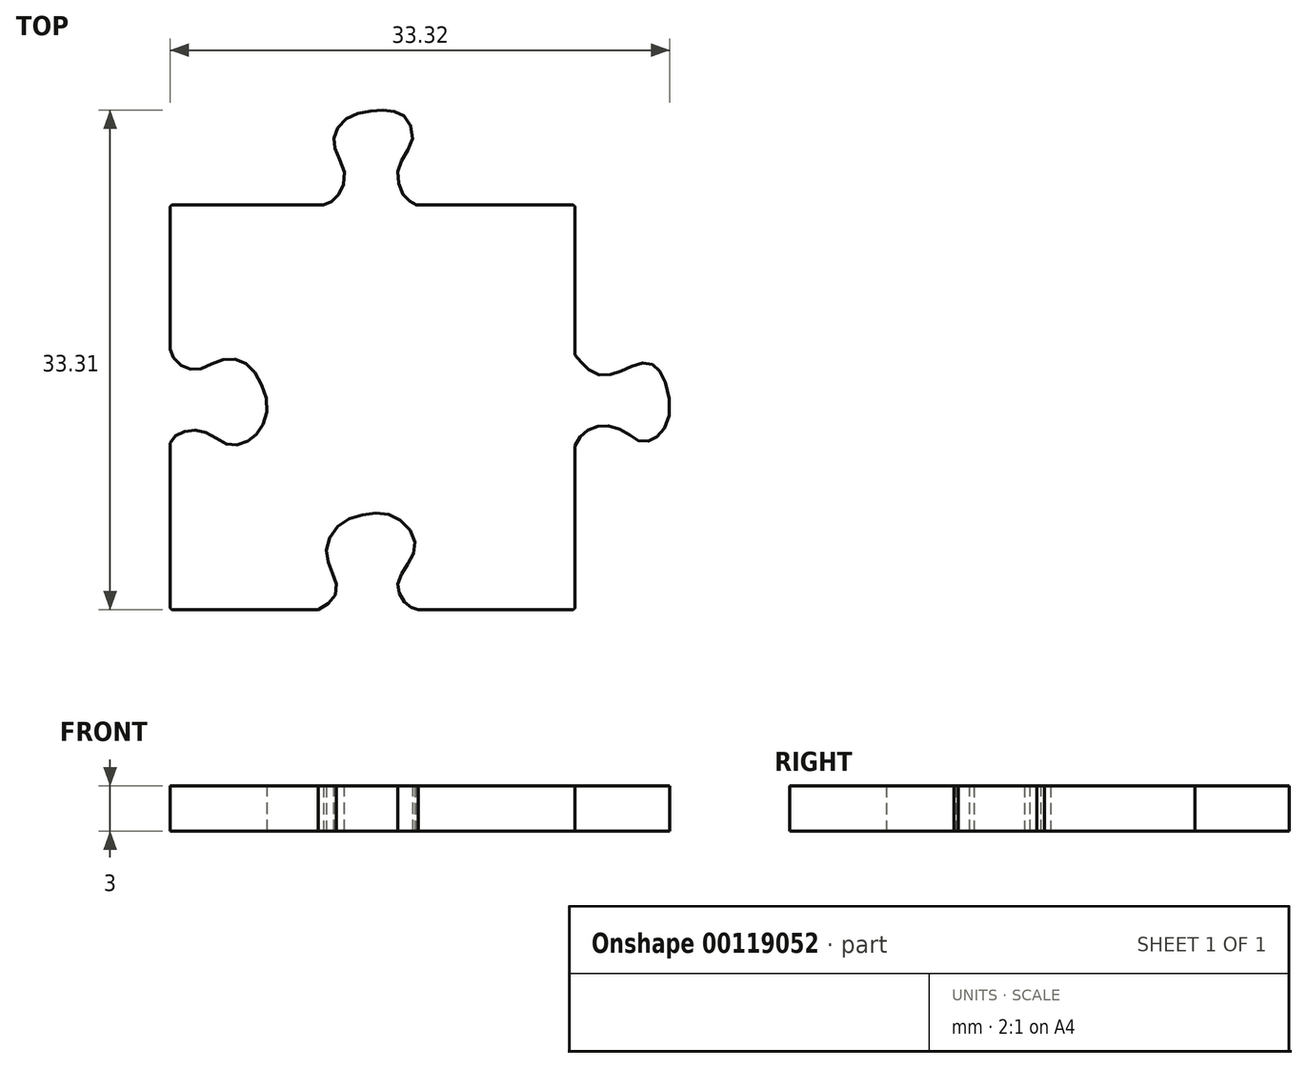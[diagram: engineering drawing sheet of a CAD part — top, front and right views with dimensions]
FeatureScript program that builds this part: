
annotation { "Feature Type Name" : "Feature", "Feature Type Description" : "" }
export const myFeature = defineFeature(function(context is Context, id is Id, definition is map)
    precondition{}
    {
        {
            var Q0;
            Q0=qCreatedBy(makeId("Top.planeOp"),FACE);
            var sketch = newSketch(context, id + "F0", { "sketchPlane" : qUnion([Q0])});
            skLineSegment(sketch, "E0.bottom", {"start": v(13.3, 13.5) * mm, "end": v(2.93, 13.5) * mm});
            skLineSegment(sketch, "E0.top", {"start": v(13.3, -13.5) * mm, "end": v(3.04, -13.5) * mm});
            skLineSegment(sketch, "E0.left", {"start": v(13.5, 13.3) * mm, "end": v(13.5, 3.49) * mm});
            skLineSegment(sketch, "E0.right", {"start": v(-13.5, 13.3) * mm, "end": v(-13.5, 3.89) * mm});
            skPoint(sketch, "E0.middle", {"position": v(0, 0) * mm});
            skFitSpline(sketch, "E1", {"points": [v(-13.5, -2.4) * mm, v(-13.06, -1.85) * mm, v(-12.19, -1.54) * mm, v(-11.23, -1.64) * mm, v(-10.18, -2.22) * mm, v(-9.3, -2.53) * mm, v(-8.23, -2.22) * mm, v(-7.52, -1.5) * mm, v(-7.03, -0.16) * mm, v(-7.37, 1.42) * mm, v(-8.21, 2.75) * mm, v(-9.3, 3.24) * mm, v(-10.53, 3) * mm, v(-11.5, 2.56) * mm, v(-12.42, 2.62) * mm, v(-13.18, 3.16) * mm, v(-13.5, 3.89) * mm], "startDerivative": vector(7.23, 11.93) * mm, "endDerivative": vector(-4.43, 14.21) * mm});
            skFitSpline(sketch, "E2", {"points": [v(-3.62, -13.5) * mm, v(-2.74, -12.9) * mm, v(-2.4, -12.05) * mm, v(-2.66, -11.08) * mm, v(-3.04, -10.02) * mm, v(-2.9, -8.8) * mm, v(-1.99, -7.67) * mm, v(-0.58, -7.14) * mm, v(0.76, -7.1) * mm, v(1.96, -7.62) * mm, v(2.79, -8.82) * mm, v(2.7, -9.8) * mm, v(2.12, -10.8) * mm, v(1.7, -11.65) * mm, v(1.76, -12.32) * mm, v(2.16, -13.02) * mm, v(2.6, -13.36) * mm, v(3.04, -13.5) * mm], "startDerivative": vector(16.2, 8.74) * mm, "endDerivative": vector(11.53, -2.8) * mm});
            skFitSpline(sketch, "E3", {"points": [v(-3.26, 13.5) * mm, v(-2.68, 13.76) * mm, v(-2.1, 14.46) * mm, v(-1.88, 15.61) * mm, v(-2.4, 17) * mm, v(-2.57, 17.9) * mm, v(-2.1, 18.93) * mm, v(-0.95, 19.6) * mm, v(0.43, 19.8) * mm, v(1.54, 19.7) * mm, v(2.37, 19.12) * mm, v(2.65, 17.8) * mm, v(2.02, 16.6) * mm, v(1.68, 15.55) * mm, v(1.92, 14.36) * mm, v(2.47, 13.75) * mm, v(2.93, 13.5) * mm], "startDerivative": vector(12.36, 4.01) * mm, "endDerivative": vector(10.48, -4.73) * mm});
            skFitSpline(sketch, "E4", {"points": [v(13.5, -2.57) * mm, v(13.97, -1.82) * mm, v(14.8, -1.34) * mm, v(15.69, -1.25) * mm, v(16.88, -1.66) * mm, v(17.63, -2.18) * mm, v(18.47, -2.24) * mm, v(19.2, -1.75) * mm, v(19.8, -0.34) * mm, v(19.4, 1.93) * mm, v(18.82, 2.75) * mm, v(18.04, 2.97) * mm, v(16.92, 2.58) * mm, v(15.97, 2.23) * mm, v(14.85, 2.24) * mm, v(13.98, 2.93) * mm, v(13.5, 3.49) * mm], "startDerivative": vector(6.76, 14.24) * mm, "endDerivative": vector(-8.43, 10.21) * mm});
            skLineSegment(sketch, "E5.trimOffspring", {"start": v(-3.26, 13.5) * mm, "end": v(-13.3, 13.5) * mm});
            skLineSegment(sketch, "E6.trimOffspring", {"start": v(13.5, -2.57) * mm, "end": v(13.5, -13.3) * mm});
            skLineSegment(sketch, "E7.trimOffspring", {"start": v(-3.62, -13.5) * mm, "end": v(-13.3, -13.5) * mm});
            skLineSegment(sketch, "E8.trimOffspring", {"start": v(-13.5, -2.4) * mm, "end": v(-13.5, -13.3) * mm});
            skPoint(sketch, "E9.visualSharp", {"position": v(-13.5, 13.5) * mm});
            skArc(sketch, "E9.filletArc", {"start": v(-13.3, 13.5) * mm, "mid": v(-13.44, 13.44) * mm, "end": v(-13.5, 13.3) * mm});
            skPoint(sketch, "E10.visualSharp", {"position": v(13.5, 13.5) * mm});
            skArc(sketch, "E10.filletArc", {"start": v(13.5, 13.3) * mm, "mid": v(13.44, 13.44) * mm, "end": v(13.3, 13.5) * mm});
            skPoint(sketch, "E11.visualSharp", {"position": v(13.5, -13.5) * mm});
            skArc(sketch, "E11.filletArc", {"start": v(13.3, -13.5) * mm, "mid": v(13.44, -13.44) * mm, "end": v(13.5, -13.3) * mm});
            skPoint(sketch, "E12.visualSharp", {"position": v(-13.5, -13.5) * mm});
            skArc(sketch, "E12.filletArc", {"start": v(-13.5, -13.3) * mm, "mid": v(-13.44, -13.44) * mm, "end": v(-13.3, -13.5) * mm});
            skSolve(sketch);
        }
        {
            var Q0;
            Q0 = qSketchRegion(id + "F0", true);
            extrude(context, id + "F1", {"entities" : qUnion([Q0]), "depth" : 3 * mm});
        }
    });
